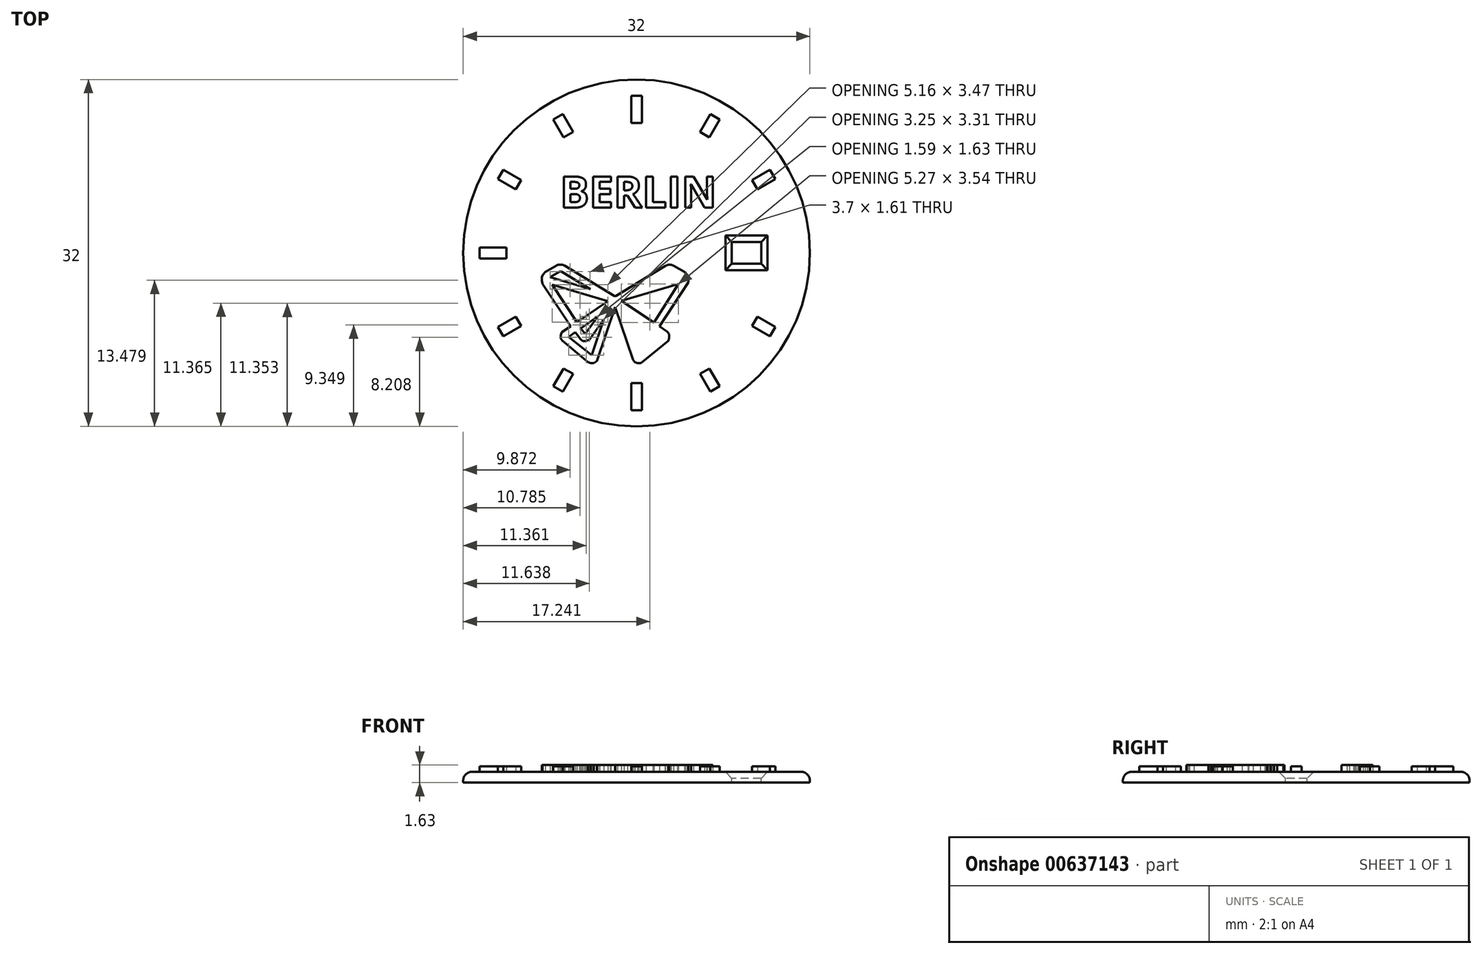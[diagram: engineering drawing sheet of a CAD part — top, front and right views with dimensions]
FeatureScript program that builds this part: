
annotation { "Feature Type Name" : "Feature", "Feature Type Description" : "" }
export const myFeature = defineFeature(function(context is Context, id is Id, definition is map)
    precondition{}
    {
        {
            var Q0;
            Q0=qCreatedBy(makeId("Top.planeOp"),FACE);
            var sketch = newSketch(context, id + "F0", { "sketchPlane" : qUnion([Q0])});
            skCircle(sketch, "E0", {"center": v(0, 0) * mm, "radius": 16 * mm});
            skLineSegment(sketch, "E1.bottom", {"start": v(8.8, 1) * mm, "end": v(11.5, 1) * mm});
            skLineSegment(sketch, "E1.top", {"start": v(8.8, -1) * mm, "end": v(11.5, -1) * mm});
            skLineSegment(sketch, "E1.left", {"start": v(8.8, 1) * mm, "end": v(8.8, -1) * mm});
            skLineSegment(sketch, "E1.right", {"start": v(11.5, 1) * mm, "end": v(11.5, -1) * mm});
            skLineSegment(sketch, "E2", {"start": v(-4.51, -9.01) * mm, "end": v(-7.42, -4.68) * mm});
            skLineSegment(sketch, "E3", {"start": v(-3.9, -8.61) * mm, "end": v(-0.72, -6.47) * mm});
            skLineSegment(sketch, "E4", {"start": v(-0.72, -6.47) * mm, "end": v(-6.45, -4.76) * mm});
            skLineSegment(sketch, "E5", {"start": v(-6.45, -4.76) * mm, "end": v(-3.9, -8.61) * mm});
            skLineSegment(sketch, "E6", {"start": v(-4.51, -9.01) * mm, "end": v(-5.44, -9.64) * mm});
            skLineSegment(sketch, "E7", {"start": v(-5.44, -9.64) * mm, "end": v(-5.54, -9.96) * mm});
            skLineSegment(sketch, "E8", {"start": v(-5.54, -9.96) * mm, "end": v(-5.54, -10.28) * mm});
            skLineSegment(sketch, "E9", {"start": v(-5.54, -10.28) * mm, "end": v(-5.38, -10.52) * mm});
            skLineSegment(sketch, "E10", {"start": v(-5.38, -10.52) * mm, "end": v(-2.76, -12.7) * mm});
            skLineSegment(sketch, "E11", {"start": v(-2.76, -12.7) * mm, "end": v(-2.48, -12.79) * mm});
            skLineSegment(sketch, "E12", {"start": v(-2.48, -12.79) * mm, "end": v(-2.15, -12.79) * mm});
            skLineSegment(sketch, "E13", {"start": v(-2.15, -12.79) * mm, "end": v(-1.84, -12.58) * mm});
            skLineSegment(sketch, "E14", {"start": v(-1.84, -12.58) * mm, "end": v(0.02, -7.06) * mm});
            skLineSegment(sketch, "E15", {"start": v(0.02, -7.06) * mm, "end": v(1.87, -12.45) * mm});
            skLineSegment(sketch, "E16", {"start": v(2.04, -12.7) * mm, "end": v(2.32, -12.79) * mm});
            skLineSegment(sketch, "E17", {"start": v(2.32, -12.79) * mm, "end": v(2.68, -12.79) * mm});
            skLineSegment(sketch, "E18", {"start": v(2.68, -12.79) * mm, "end": v(5.48, -10.52) * mm});
            skLineSegment(sketch, "E19", {"start": v(5.48, -10.52) * mm, "end": v(5.57, -10.22) * mm});
            skLineSegment(sketch, "E20", {"start": v(5.57, -10.22) * mm, "end": v(5.57, -9.85) * mm});
            skLineSegment(sketch, "E21", {"start": v(5.57, -9.85) * mm, "end": v(5.4, -9.58) * mm});
            skLineSegment(sketch, "E22", {"start": v(5.4, -9.58) * mm, "end": v(4.59, -9.01) * mm});
            skLineSegment(sketch, "E23", {"start": v(4.59, -9.01) * mm, "end": v(7.53, -4.5) * mm});
            skLineSegment(sketch, "E24", {"start": v(7.53, -4.5) * mm, "end": v(7.53, -4.14) * mm});
            skLineSegment(sketch, "E25", {"start": v(7.53, -4.14) * mm, "end": v(7.4, -3.8) * mm});
            skLineSegment(sketch, "E26", {"start": v(7.4, -3.8) * mm, "end": v(7.17, -3.47) * mm});
            skLineSegment(sketch, "E27", {"start": v(7.17, -3.47) * mm, "end": v(6.04, -2.83) * mm});
            skLineSegment(sketch, "E28", {"start": v(6.04, -2.83) * mm, "end": v(5.8, -2.7) * mm});
            skLineSegment(sketch, "E29", {"start": v(5.8, -2.7) * mm, "end": v(5.47, -2.7) * mm});
            skLineSegment(sketch, "E30", {"start": v(5.47, -2.7) * mm, "end": v(5.14, -2.84) * mm});
            skLineSegment(sketch, "E31", {"start": v(5.14, -2.84) * mm, "end": v(0.1, -5.92) * mm});
            skLineSegment(sketch, "E32", {"start": v(0.1, -5.92) * mm, "end": v(-0.04, -5.92) * mm});
            skLineSegment(sketch, "E33", {"start": v(-0.04, -5.92) * mm, "end": v(-5.14, -2.83) * mm});
            skLineSegment(sketch, "E34", {"start": v(-5.14, -2.83) * mm, "end": v(-5.37, -2.73) * mm});
            skLineSegment(sketch, "E35", {"start": v(-5.82, -2.73) * mm, "end": v(-7.14, -3.45) * mm});
            skLineSegment(sketch, "E36", {"start": v(-7.14, -3.45) * mm, "end": v(-7.4, -3.73) * mm});
            skLineSegment(sketch, "E37", {"start": v(-7.4, -3.73) * mm, "end": v(-7.5, -4) * mm});
            skLineSegment(sketch, "E38", {"start": v(-7.5, -4) * mm, "end": v(-7.5, -4.33) * mm});
            skLineSegment(sketch, "E39", {"start": v(-7.5, -4.33) * mm, "end": v(-7.42, -4.68) * mm});
            skLineSegment(sketch, "E40", {"start": v(-2.53, -5.2) * mm, "end": v(-6.64, -4) * mm});
            skLineSegment(sketch, "E41", {"start": v(-6.64, -4) * mm, "end": v(-5.65, -3.42) * mm});
            skLineSegment(sketch, "E42", {"start": v(-5.65, -3.42) * mm, "end": v(-5.47, -3.42) * mm});
            skLineSegment(sketch, "E43", {"start": v(-5.47, -3.42) * mm, "end": v(-2.53, -5.2) * mm});
            skLineSegment(sketch, "E44", {"start": v(0.76, -6.46) * mm, "end": v(6.62, -4.75) * mm});
            skLineSegment(sketch, "E45", {"start": v(6.62, -4.75) * mm, "end": v(4.1, -8.68) * mm});
            skLineSegment(sketch, "E46", {"start": v(4.1, -8.68) * mm, "end": v(0.76, -6.46) * mm});
            skLineSegment(sketch, "E47", {"start": v(-1.74, -7.99) * mm, "end": v(-3.04, -9.8) * mm});
            skLineSegment(sketch, "E48", {"start": v(-3.04, -9.8) * mm, "end": v(-3.52, -9.22) * mm});
            skLineSegment(sketch, "E49", {"start": v(-3.52, -9.22) * mm, "end": v(-1.74, -7.99) * mm});
            skLineSegment(sketch, "E50", {"start": v(-1.12, -8.33) * mm, "end": v(-2.36, -12) * mm});
            skLineSegment(sketch, "E51", {"start": v(-2.36, -12) * mm, "end": v(-4.74, -10.12) * mm});
            skLineSegment(sketch, "E52", {"start": v(-4.74, -10.12) * mm, "end": v(-4.07, -9.61) * mm});
            skLineSegment(sketch, "E53", {"start": v(-4.07, -9.61) * mm, "end": v(-3.5, -10.36) * mm});
            skLineSegment(sketch, "E54", {"start": v(-3.5, -10.36) * mm, "end": v(-3.27, -10.54) * mm});
            skLineSegment(sketch, "E55", {"start": v(-3.27, -10.54) * mm, "end": v(-2.97, -10.54) * mm});
            skLineSegment(sketch, "E56", {"start": v(-2.97, -10.54) * mm, "end": v(-2.59, -10.36) * mm});
            skLineSegment(sketch, "E57", {"start": v(-2.59, -10.36) * mm, "end": v(-1.12, -8.33) * mm});
            skLineSegment(sketch, "E58", {"start": v(-5.82, -2.73) * mm, "end": v(-5.37, -2.73) * mm});
            skLineSegment(sketch, "E59", {"start": v(0, 0) * mm, "end": v(0, 16) * mm});
            skText(sketch, "E60", { "text": "BERLIN", "fontName": "OpenSans-Bold.ttf"});
            const initialGuessF0  = {"E60": [-0.01023, 0.00388, 1, 0, 0.00412]};
            skSetInitialGuess(sketch, initialGuessF0);
            skSolve(sketch);
        }
        {
            var Q0;
            Q0=makeQuery(id+"F0.imprint","IMPRINT",FACE,{"disambiguationData":[TD([[makeQuery(id+"F0.imprint","IMPRINT",EDGE,{"derivedFrom":sQuery(id+"F0.wireOp",EDGE,"E0")}),1.0]])]});
            var Q1;
            Q1=makeQuery(id+"F0.imprint","IMPRINT",FACE,{"disambiguationData":[TD([[makeQuery(id+"F0.imprint","IMPRINT",EDGE,{"derivedFrom":sQuery(id+"F0.wireOp",EDGE,"E60.sketch_text.stroke-66")}),-1.0]])]});
            var Q2;
            Q2=makeQuery(id+"F0.imprint","IMPRINT",FACE,{"disambiguationData":[TD([[makeQuery(id+"F0.imprint","IMPRINT",EDGE,{"derivedFrom":sQuery(id+"F0.wireOp",EDGE,"E50")}),-1.0]])]});
            var Q3;
            Q3=makeQuery(id+"F0.imprint","IMPRINT",FACE,{"disambiguationData":[TD([[makeQuery(id+"F0.imprint","IMPRINT",EDGE,{"derivedFrom":sQuery(id+"F0.wireOp",EDGE,"E60.sketch_text.stroke-0")}),-1.0]])]});
            var Q4;
            Q4=makeQuery(id+"F0.imprint","IMPRINT",FACE,{"disambiguationData":[TD([[makeQuery(id+"F0.imprint","IMPRINT",EDGE,{"derivedFrom":sQuery(id+"F0.wireOp",EDGE,"E3")}),1.0]])]});
            var Q5;
            Q5=makeQuery(id+"F0.imprint","IMPRINT",FACE,{"disambiguationData":[TD([[makeQuery(id+"F0.imprint","IMPRINT",EDGE,{"derivedFrom":sQuery(id+"F0.wireOp",EDGE,"E40")}),-1.0]])]});
            var Q6;
            Q6=makeQuery(id+"F0.imprint","IMPRINT",FACE,{"disambiguationData":[TD([[makeQuery(id+"F0.imprint","IMPRINT",EDGE,{"derivedFrom":sQuery(id+"F0.wireOp",EDGE,"E60.sketch_text.stroke-12")}),1.0]])]});
            var Q7;
            {var subQ5=sQuery(id+"F0.wireOp",EDGE,"E60.sketch_text.stroke-51");Q7=makeQuery(id+"F0.imprint","IMPRINT",FACE,{"disambiguationData":[TD([[makeQuery(id+"F0.imprint","IMPRINT",EDGE,{"derivedFrom":subQ5}),1.0]])]});}
            var Q8;
            Q8=makeQuery(id+"F0.imprint","IMPRINT",FACE,{"disambiguationData":[TD([[makeQuery(id+"F0.imprint","IMPRINT",EDGE,{"derivedFrom":sQuery(id+"F0.wireOp",EDGE,"E60.sketch_text.stroke-56")}),-1.0]])]});
            var Q9;
            Q9=makeQuery(id+"F0.imprint","IMPRINT",FACE,{"disambiguationData":[TD([[makeQuery(id+"F0.imprint","IMPRINT",EDGE,{"derivedFrom":sQuery(id+"F0.wireOp",EDGE,"E60.sketch_text.stroke-62")}),-1.0]])]});
            var Q10;
            Q10=makeQuery(id+"F0.imprint","IMPRINT",FACE,{"disambiguationData":[TD([[makeQuery(id+"F0.imprint","IMPRINT",EDGE,{"derivedFrom":sQuery(id+"F0.wireOp",EDGE,"E60.sketch_text.stroke-25")}),-1.0]])]});
            var Q11;
            Q11=makeQuery(id+"F0.imprint","IMPRINT",FACE,{"disambiguationData":[TD([[makeQuery(id+"F0.imprint","IMPRINT",EDGE,{"derivedFrom":sQuery(id+"F0.wireOp",EDGE,"E60.sketch_text.stroke-37")}),-1.0]])]});
            var Q12;
            Q12=makeQuery(id+"F0.imprint","IMPRINT",FACE,{"disambiguationData":[TD([[makeQuery(id+"F0.imprint","IMPRINT",EDGE,{"derivedFrom":sQuery(id+"F0.wireOp",EDGE,"E60.sketch_text.stroke-19")}),1.0]])]});
            var Q13;
            Q13=makeQuery(id+"F0.imprint","IMPRINT",FACE,{"disambiguationData":[TD([[makeQuery(id+"F0.imprint","IMPRINT",EDGE,{"derivedFrom":sQuery(id+"F0.wireOp",EDGE,"E60.sketch_text.stroke-37")}),1.0]])]});
            var Q14;
            Q14=makeQuery(id+"F0.imprint","IMPRINT",FACE,{"disambiguationData":[TD([[makeQuery(id+"F0.imprint","IMPRINT",EDGE,{"derivedFrom":sQuery(id+"F0.wireOp",EDGE,"E44")}),-1.0]])]});
            var Q15;
            Q15=makeQuery(id+"F0.imprint","IMPRINT",FACE,{"disambiguationData":[TD([[makeQuery(id+"F0.imprint","IMPRINT",EDGE,{"derivedFrom":sQuery(id+"F0.wireOp",EDGE,"E47")}),-1.0]])]});
            var Q16;
            {var subQ0=sQuery(id+"F0.wireOp",EDGE,"E60.sketch_text.stroke-49");var subQ1=sQuery(id+"F0.wireOp",EDGE,"E59");var subQ2=makeQuery(id+"F0.imprint","INTERSECT",VERTEX,{"derivedFrom":[subQ1,subQ0]});Q16=makeQuery(id+"F0.imprint","IMPRINT",FACE,{"disambiguationData":[TD([[makeQuery(id+"F0.imprint","IMPRINT",EDGE,{"disambiguationData":[TD([[subQ2,1.0]])],"derivedFrom":subQ1}),-1.0]])]});}
            var Q17;
            {var subQ0=sQuery(id+"F0.wireOp",EDGE,"E60.sketch_text.stroke-53");var subQ1=sQuery(id+"F0.wireOp",EDGE,"E59");var subQ2=makeQuery(id+"F0.imprint","INTERSECT",VERTEX,{"derivedFrom":[subQ1,subQ0]});Q17=makeQuery(id+"F0.imprint","IMPRINT",FACE,{"disambiguationData":[TD([[makeQuery(id+"F0.imprint","IMPRINT",EDGE,{"disambiguationData":[TD([[subQ2,-1.0]])],"derivedFrom":subQ1}),-1.0]])]});}
            extrude(context, id + "F1", {"entities" : qUnion([Q0, Q1, Q2, Q3, Q4, Q5, Q6, Q7, Q8, Q9, Q10, Q11, Q12, Q13, Q14, Q15, Q16, Q17]), "oppositeDirection" : true, "depth" : 1 * mm, "offsetDistance" : 25 * mm});
        }
        {
            var Q0;
            Q0=qCreatedBy(makeId("Top.planeOp"),FACE);
            var sketch = newSketch(context, id + "F2", { "sketchPlane" : qUnion([Q0])});
            skLineSegment(sketch, "E61", {"start": v(-6.74, -7.5) * mm, "end": v(-9.65, -3.17) * mm});
            skLineSegment(sketch, "E62", {"start": v(-6.1, -7.1) * mm, "end": v(-2.93, -4.95) * mm});
            skLineSegment(sketch, "E63", {"start": v(-2.93, -4.95) * mm, "end": v(-8.66, -3.24) * mm});
            skLineSegment(sketch, "E64", {"start": v(-8.66, -3.24) * mm, "end": v(-6.1, -7.1) * mm});
            skLineSegment(sketch, "E65", {"start": v(-6.74, -7.5) * mm, "end": v(-7.67, -8.13) * mm});
            skLineSegment(sketch, "E66", {"start": v(-7.67, -8.13) * mm, "end": v(-7.76, -8.45) * mm});
            skLineSegment(sketch, "E67", {"start": v(-7.76, -8.45) * mm, "end": v(-7.76, -8.78) * mm});
            skLineSegment(sketch, "E68", {"start": v(-7.76, -8.78) * mm, "end": v(-7.6, -9) * mm});
            skLineSegment(sketch, "E69", {"start": v(-7.6, -9) * mm, "end": v(-4.99, -11.2) * mm});
            skLineSegment(sketch, "E70", {"start": v(-4.99, -11.2) * mm, "end": v(-4.7, -11.28) * mm});
            skLineSegment(sketch, "E71", {"start": v(-4.7, -11.28) * mm, "end": v(-4.37, -11.28) * mm});
            skLineSegment(sketch, "E72", {"start": v(-4.37, -11.28) * mm, "end": v(-4.06, -11.07) * mm});
            skLineSegment(sketch, "E73", {"start": v(-4.06, -11.07) * mm, "end": v(-2.2, -5.55) * mm});
            skLineSegment(sketch, "E74", {"start": v(-2.2, -5.55) * mm, "end": v(-0.36, -10.94) * mm});
            skLineSegment(sketch, "E75", {"start": v(-0.19, -11.2) * mm, "end": v(0.1, -11.28) * mm});
            skLineSegment(sketch, "E76", {"start": v(0.1, -11.28) * mm, "end": v(0.45, -11.28) * mm});
            skLineSegment(sketch, "E77", {"start": v(0.45, -11.28) * mm, "end": v(3.26, -9) * mm});
            skLineSegment(sketch, "E78", {"start": v(3.26, -9) * mm, "end": v(3.35, -8.71) * mm});
            skLineSegment(sketch, "E79", {"start": v(3.35, -8.71) * mm, "end": v(3.35, -8.34) * mm});
            skLineSegment(sketch, "E80", {"start": v(3.35, -8.34) * mm, "end": v(3.17, -8.07) * mm});
            skLineSegment(sketch, "E81", {"start": v(3.17, -8.07) * mm, "end": v(2.36, -7.5) * mm});
            skLineSegment(sketch, "E82", {"start": v(2.36, -7.5) * mm, "end": v(5.3, -3) * mm});
            skLineSegment(sketch, "E83", {"start": v(5.3, -3) * mm, "end": v(5.3, -2.63) * mm});
            skLineSegment(sketch, "E84", {"start": v(5.3, -2.63) * mm, "end": v(5.17, -2.29) * mm});
            skLineSegment(sketch, "E85", {"start": v(5.17, -2.29) * mm, "end": v(4.94, -1.96) * mm});
            skLineSegment(sketch, "E86", {"start": v(4.94, -1.96) * mm, "end": v(3.8, -1.32) * mm});
            skLineSegment(sketch, "E87", {"start": v(3.8, -1.32) * mm, "end": v(3.57, -1.2) * mm});
            skLineSegment(sketch, "E88", {"start": v(3.57, -1.2) * mm, "end": v(3.24, -1.2) * mm});
            skLineSegment(sketch, "E89", {"start": v(3.24, -1.2) * mm, "end": v(2.91, -1.33) * mm});
            skLineSegment(sketch, "E90", {"start": v(2.91, -1.33) * mm, "end": v(-2.12, -4.41) * mm});
            skLineSegment(sketch, "E91", {"start": v(-2.12, -4.41) * mm, "end": v(-2.27, -4.41) * mm});
            skLineSegment(sketch, "E92", {"start": v(-2.27, -4.41) * mm, "end": v(-7.37, -1.32) * mm});
            skLineSegment(sketch, "E93", {"start": v(-7.37, -1.32) * mm, "end": v(-7.6, -1.21) * mm});
            skLineSegment(sketch, "E94", {"start": v(-8.05, -1.21) * mm, "end": v(-9.37, -1.94) * mm});
            skLineSegment(sketch, "E95", {"start": v(-9.37, -1.94) * mm, "end": v(-9.62, -2.22) * mm});
            skLineSegment(sketch, "E96", {"start": v(-9.62, -2.22) * mm, "end": v(-9.73, -2.49) * mm});
            skLineSegment(sketch, "E97", {"start": v(-9.73, -2.49) * mm, "end": v(-9.73, -2.83) * mm});
            skLineSegment(sketch, "E98", {"start": v(-9.73, -2.83) * mm, "end": v(-9.65, -3.17) * mm});
            skLineSegment(sketch, "E99", {"start": v(-4.76, -3.7) * mm, "end": v(-8.86, -2.49) * mm});
            skLineSegment(sketch, "E100", {"start": v(-8.86, -2.49) * mm, "end": v(-7.87, -1.9) * mm});
            skLineSegment(sketch, "E101", {"start": v(-7.87, -1.9) * mm, "end": v(-7.7, -1.9) * mm});
            skLineSegment(sketch, "E102", {"start": v(-7.7, -1.9) * mm, "end": v(-4.76, -3.7) * mm});
            skLineSegment(sketch, "E103", {"start": v(-1.55, -4.9) * mm, "end": v(4.3, -3.18) * mm});
            skLineSegment(sketch, "E104", {"start": v(4.3, -3.18) * mm, "end": v(1.78, -7.12) * mm});
            skLineSegment(sketch, "E105", {"start": v(1.78, -7.12) * mm, "end": v(-1.55, -4.9) * mm});
            skLineSegment(sketch, "E106", {"start": v(-3.96, -6.49) * mm, "end": v(-5.26, -8.3) * mm});
            skLineSegment(sketch, "E107", {"start": v(-5.26, -8.3) * mm, "end": v(-5.73, -7.72) * mm});
            skLineSegment(sketch, "E108", {"start": v(-5.73, -7.72) * mm, "end": v(-3.96, -6.49) * mm});
            skLineSegment(sketch, "E109", {"start": v(-3.35, -6.82) * mm, "end": v(-4.58, -10.5) * mm});
            skLineSegment(sketch, "E110", {"start": v(-4.58, -10.5) * mm, "end": v(-6.96, -8.61) * mm});
            skLineSegment(sketch, "E111", {"start": v(-6.96, -8.61) * mm, "end": v(-6.3, -8.1) * mm});
            skLineSegment(sketch, "E112", {"start": v(-6.3, -8.1) * mm, "end": v(-5.73, -8.85) * mm});
            skLineSegment(sketch, "E113", {"start": v(-5.73, -8.85) * mm, "end": v(-5.5, -9.03) * mm});
            skLineSegment(sketch, "E114", {"start": v(-5.5, -9.03) * mm, "end": v(-5.2, -9.03) * mm});
            skLineSegment(sketch, "E115", {"start": v(-5.2, -9.03) * mm, "end": v(-4.81, -8.85) * mm});
            skLineSegment(sketch, "E116", {"start": v(-4.81, -8.85) * mm, "end": v(-3.35, -6.82) * mm});
            skLineSegment(sketch, "E117", {"start": v(-8.05, -1.21) * mm, "end": v(-7.6, -1.21) * mm});
            skText(sketch, "E118", { "text": "BERLIN", "fontName": "OpenSans-Bold.ttf"});
            skLineSegment(sketch, "E119", {"start": v(-0.19, -11.2) * mm, "end": v(-0.36, -10.94) * mm});
            const initialGuessF2  = {"E118": [-0.00787, 0.00465, 1, 0, 0.00322]};
            skSetInitialGuess(sketch, initialGuessF2);
            skSolve(sketch);
        }
        {
            var Q0;
            Q0 = qSketchRegion(id + "F2", true);
            extrude(context, id + "F3", {"entities" : qUnion([Q0]), "depth" : 0.7 * mm, "offsetDistance" : 25 * mm});
        }
        {
            var Q0;
            Q0=makeQuery(id+"F1.opExtrude","CAP_EDGE",EDGE,{"disambiguationData":[OSD([sQuery(id+"F0.wireOp",EDGE,"E1.bottom")])],"isStart":true});
            var Q1;
            Q1=makeQuery(id+"F1.opExtrude","CAP_EDGE",EDGE,{"disambiguationData":[OSD([sQuery(id+"F0.wireOp",EDGE,"E1.left")])],"isStart":true});
            var Q2;
            Q2=makeQuery(id+"F1.opExtrude","CAP_EDGE",EDGE,{"disambiguationData":[OSD([sQuery(id+"F0.wireOp",EDGE,"E1.right")])],"isStart":true});
            var Q3;
            Q3=makeQuery(id+"F1.opExtrude","CAP_EDGE",EDGE,{"disambiguationData":[OSD([sQuery(id+"F0.wireOp",EDGE,"E1.top")])],"isStart":true});
            chamfer(context, id + "F4", {"entities" : qUnion([Q0, Q1, Q2, Q3]), "width" : 0.6 * mm, "tangentPropagation" : true});
        }
        {
            var Q0;
            Q0=makeQuery(id+"F1.opExtrude","CAP_EDGE",EDGE,{"disambiguationData":[OSD([sQuery(id+"F0.wireOp",EDGE,"E0")])],"isStart":true});
            fillet(context, id + "F5", {"entities" : qUnion([Q0]), "radius" : 0.8 * mm, "tangentPropagation" : true, "allowEdgeOverflow" : false});
        }
        {
            var Q0;
            Q0=qCreatedBy(makeId("Top.planeOp"),FACE);
            var sketch = newSketch(context, id + "F6", { "sketchPlane" : qUnion([Q0])});
            skCircle(sketch, "E120.0", {"center": v(0, 0) * mm, "radius": 12 * mm});
            skCircle(sketch, "E121.0", {"center": v(0, 0) * mm, "radius": 14.5 * mm});
            skLineSegment(sketch, "E122.0", {"start": v(-12, 0.5) * mm, "end": v(-14.5, 0.5) * mm});
            skLineSegment(sketch, "E123.0", {"start": v(-12, -0.5) * mm, "end": v(-14.5, -0.5) * mm});
            skLineSegment(sketch, "E124", {"start": v(-12, 0.5) * mm, "end": v(-12, -0.5) * mm});
            skLineSegment(sketch, "E125", {"start": v(-14.5, 0.5) * mm, "end": v(-14.5, -0.5) * mm});
            skLineSegment(sketch, "E126.0", {"start": v(0.5, 12) * mm, "end": v(0.5, 14.5) * mm});
            skLineSegment(sketch, "E127.0", {"start": v(-0.5, 12) * mm, "end": v(-0.5, 14.5) * mm});
            skLineSegment(sketch, "E128", {"start": v(-0.5, 14.5) * mm, "end": v(0.5, 14.5) * mm});
            skLineSegment(sketch, "E129", {"start": v(-0.5, 12) * mm, "end": v(0.5, 12) * mm});
            skLineSegment(sketch, "E130.0", {"start": v(0.5, -14.5) * mm, "end": v(0.5, -12) * mm});
            skLineSegment(sketch, "E131.0", {"start": v(-0.5, -14.5) * mm, "end": v(-0.5, -12) * mm});
            skLineSegment(sketch, "E132", {"start": v(-0.5, -12) * mm, "end": v(0.5, -12) * mm});
            skLineSegment(sketch, "E133", {"start": v(-0.5, -14.5) * mm, "end": v(0.5, -14.5) * mm});
            skCircle(sketch, "E134.0", {"center": v(0, 0) * mm, "radius": 12.6 * mm});
            skLineSegment(sketch, "E135.0", {"start": v(-5.87, -11.16) * mm, "end": v(-6.82, -12.8) * mm});
            skLineSegment(sketch, "E136.0", {"start": v(-6.73, -10.66) * mm, "end": v(-7.68, -12.3) * mm});
            skLineSegment(sketch, "E137.0", {"start": v(-11.16, -5.87) * mm, "end": v(-12.8, -6.82) * mm});
            skLineSegment(sketch, "E138.0", {"start": v(-10.66, -6.73) * mm, "end": v(-12.3, -7.68) * mm});
            skLineSegment(sketch, "E139", {"start": v(-12.3, -7.68) * mm, "end": v(-12.8, -6.82) * mm});
            skLineSegment(sketch, "E140", {"start": v(-11.16, -5.87) * mm, "end": v(-10.66, -6.73) * mm});
            skLineSegment(sketch, "E141", {"start": v(-7.68, -12.3) * mm, "end": v(-6.82, -12.8) * mm});
            skLineSegment(sketch, "E142", {"start": v(-6.73, -10.66) * mm, "end": v(-5.87, -11.16) * mm});
            skLineSegment(sketch, "E143", {"start": v(-6.82, -12.8) * mm, "end": v(-7.68, -12.3) * mm});
            skLineSegment(sketch, "E144.0", {"start": v(5.87, -11.16) * mm, "end": v(6.82, -12.8) * mm});
            skLineSegment(sketch, "E145.0", {"start": v(6.73, -10.66) * mm, "end": v(7.68, -12.3) * mm});
            skLineSegment(sketch, "E146.0", {"start": v(10.66, -6.73) * mm, "end": v(12.3, -7.68) * mm});
            skLineSegment(sketch, "E147.0", {"start": v(11.16, -5.87) * mm, "end": v(12.8, -6.82) * mm});
            skLineSegment(sketch, "E148.0", {"start": v(6.73, 10.66) * mm, "end": v(7.68, 12.3) * mm});
            skLineSegment(sketch, "E149.0", {"start": v(5.87, 11.16) * mm, "end": v(6.82, 12.8) * mm});
            skLineSegment(sketch, "E150.0", {"start": v(11.16, 5.87) * mm, "end": v(12.8, 6.82) * mm});
            skLineSegment(sketch, "E151.0", {"start": v(10.66, 6.73) * mm, "end": v(12.3, 7.68) * mm});
            skLineSegment(sketch, "E152.0", {"start": v(-5.87, 11.16) * mm, "end": v(-6.82, 12.8) * mm});
            skLineSegment(sketch, "E153.0", {"start": v(-6.73, 10.66) * mm, "end": v(-7.68, 12.3) * mm});
            skLineSegment(sketch, "E154.0", {"start": v(-10.66, 6.73) * mm, "end": v(-12.3, 7.68) * mm});
            skLineSegment(sketch, "E155.0", {"start": v(-11.16, 5.87) * mm, "end": v(-12.8, 6.82) * mm});
            skLineSegment(sketch, "E156", {"start": v(-12.8, 6.82) * mm, "end": v(-12.3, 7.68) * mm});
            skLineSegment(sketch, "E157", {"start": v(-11.16, 5.87) * mm, "end": v(-10.66, 6.73) * mm});
            skLineSegment(sketch, "E158", {"start": v(-7.68, 12.3) * mm, "end": v(-6.82, 12.8) * mm});
            skLineSegment(sketch, "E159", {"start": v(-6.73, 10.66) * mm, "end": v(-5.87, 11.16) * mm});
            skLineSegment(sketch, "E160", {"start": v(5.87, 11.16) * mm, "end": v(6.73, 10.66) * mm});
            skLineSegment(sketch, "E161", {"start": v(6.82, 12.8) * mm, "end": v(7.68, 12.3) * mm});
            skLineSegment(sketch, "E162", {"start": v(10.66, 6.73) * mm, "end": v(11.16, 5.87) * mm});
            skLineSegment(sketch, "E163", {"start": v(12.3, 7.68) * mm, "end": v(12.8, 6.82) * mm});
            skLineSegment(sketch, "E164", {"start": v(11.16, -5.87) * mm, "end": v(10.66, -6.73) * mm});
            skLineSegment(sketch, "E165", {"start": v(12.3, -7.68) * mm, "end": v(12.8, -6.82) * mm});
            skLineSegment(sketch, "E166", {"start": v(5.87, -11.16) * mm, "end": v(6.73, -10.66) * mm});
            skLineSegment(sketch, "E167", {"start": v(6.82, -12.8) * mm, "end": v(7.68, -12.3) * mm});
            skSolve(sketch);
        }
        {
            var Q0;
            Q0=makeQuery(id+"F3.opExtrude","SWEPT_BODY",BODY,{"disambiguationData":[OSD([sQuery(id+"F2.wireOp",EDGE,"E61"),sQuery(id+"F2.wireOp",EDGE,"E62"),sQuery(id+"F2.wireOp",EDGE,"E63"),sQuery(id+"F2.wireOp",EDGE,"E64"),sQuery(id+"F2.wireOp",EDGE,"E65"),sQuery(id+"F2.wireOp",EDGE,"E66"),sQuery(id+"F2.wireOp",EDGE,"E67"),sQuery(id+"F2.wireOp",EDGE,"E68"),sQuery(id+"F2.wireOp",EDGE,"E69"),sQuery(id+"F2.wireOp",EDGE,"E70"),sQuery(id+"F2.wireOp",EDGE,"E71"),sQuery(id+"F2.wireOp",EDGE,"E72"),sQuery(id+"F2.wireOp",EDGE,"E73"),sQuery(id+"F2.wireOp",EDGE,"E74"),sQuery(id+"F2.wireOp",EDGE,"E75"),sQuery(id+"F2.wireOp",EDGE,"E76"),sQuery(id+"F2.wireOp",EDGE,"E77"),sQuery(id+"F2.wireOp",EDGE,"E78"),sQuery(id+"F2.wireOp",EDGE,"E79"),sQuery(id+"F2.wireOp",EDGE,"E80"),sQuery(id+"F2.wireOp",EDGE,"E81"),sQuery(id+"F2.wireOp",EDGE,"E82"),sQuery(id+"F2.wireOp",EDGE,"E83"),sQuery(id+"F2.wireOp",EDGE,"E84"),sQuery(id+"F2.wireOp",EDGE,"E85"),sQuery(id+"F2.wireOp",EDGE,"E86"),sQuery(id+"F2.wireOp",EDGE,"E87"),sQuery(id+"F2.wireOp",EDGE,"E88"),sQuery(id+"F2.wireOp",EDGE,"E89"),sQuery(id+"F2.wireOp",EDGE,"E90"),sQuery(id+"F2.wireOp",EDGE,"E91"),sQuery(id+"F2.wireOp",EDGE,"E92"),sQuery(id+"F2.wireOp",EDGE,"E93"),sQuery(id+"F2.wireOp",EDGE,"E94"),sQuery(id+"F2.wireOp",EDGE,"E95"),sQuery(id+"F2.wireOp",EDGE,"E96"),sQuery(id+"F2.wireOp",EDGE,"E97"),sQuery(id+"F2.wireOp",EDGE,"E98"),sQuery(id+"F2.wireOp",EDGE,"E99"),sQuery(id+"F2.wireOp",EDGE,"E100"),sQuery(id+"F2.wireOp",EDGE,"E101"),sQuery(id+"F2.wireOp",EDGE,"E102"),sQuery(id+"F2.wireOp",EDGE,"E103"),sQuery(id+"F2.wireOp",EDGE,"E104"),sQuery(id+"F2.wireOp",EDGE,"E105"),sQuery(id+"F2.wireOp",EDGE,"E106"),sQuery(id+"F2.wireOp",EDGE,"E107"),sQuery(id+"F2.wireOp",EDGE,"E108"),sQuery(id+"F2.wireOp",EDGE,"E109"),sQuery(id+"F2.wireOp",EDGE,"E110"),sQuery(id+"F2.wireOp",EDGE,"E111"),sQuery(id+"F2.wireOp",EDGE,"E112"),sQuery(id+"F2.wireOp",EDGE,"E113"),sQuery(id+"F2.wireOp",EDGE,"E114"),sQuery(id+"F2.wireOp",EDGE,"E115"),sQuery(id+"F2.wireOp",EDGE,"E116"),sQuery(id+"F2.wireOp",EDGE,"E117"),sQuery(id+"F2.wireOp",EDGE,"E119")])]});
            var Q1;
            Q1=qCreatedBy(makeId("Origin.pointOp"),VERTEX);
            transform(context, id + "F7", {"entities" : qUnion([Q0]), "transformType" : TransformType.SCALE_UNIFORMLY, "scale" : 0.9, "scalePoint" : qUnion([Q1]), "makeCopy" : false});
        }
        {
            var Q0;
            Q0=makeQuery(id+"F3.opExtrude","SWEPT_BODY",BODY,{"disambiguationData":[OSD([sQuery(id+"F2.wireOp",EDGE,"E118.sketch_text.stroke-0"),sQuery(id+"F2.wireOp",EDGE,"E118.sketch_text.stroke-1"),sQuery(id+"F2.wireOp",EDGE,"E118.sketch_text.stroke-2"),sQuery(id+"F2.wireOp",EDGE,"E118.sketch_text.stroke-3"),sQuery(id+"F2.wireOp",EDGE,"E118.sketch_text.stroke-4"),sQuery(id+"F2.wireOp",EDGE,"E118.sketch_text.stroke-5"),sQuery(id+"F2.wireOp",EDGE,"E118.sketch_text.stroke-6"),sQuery(id+"F2.wireOp",EDGE,"E118.sketch_text.stroke-7"),sQuery(id+"F2.wireOp",EDGE,"E118.sketch_text.stroke-8"),sQuery(id+"F2.wireOp",EDGE,"E118.sketch_text.stroke-9"),sQuery(id+"F2.wireOp",EDGE,"E118.sketch_text.stroke-10"),sQuery(id+"F2.wireOp",EDGE,"E118.sketch_text.stroke-11"),sQuery(id+"F2.wireOp",EDGE,"E118.sketch_text.stroke-12"),sQuery(id+"F2.wireOp",EDGE,"E118.sketch_text.stroke-13"),sQuery(id+"F2.wireOp",EDGE,"E118.sketch_text.stroke-14"),sQuery(id+"F2.wireOp",EDGE,"E118.sketch_text.stroke-15"),sQuery(id+"F2.wireOp",EDGE,"E118.sketch_text.stroke-16"),sQuery(id+"F2.wireOp",EDGE,"E118.sketch_text.stroke-17"),sQuery(id+"F2.wireOp",EDGE,"E118.sketch_text.stroke-18"),sQuery(id+"F2.wireOp",EDGE,"E118.sketch_text.stroke-19"),sQuery(id+"F2.wireOp",EDGE,"E118.sketch_text.stroke-20"),sQuery(id+"F2.wireOp",EDGE,"E118.sketch_text.stroke-21"),sQuery(id+"F2.wireOp",EDGE,"E118.sketch_text.stroke-22"),sQuery(id+"F2.wireOp",EDGE,"E118.sketch_text.stroke-23"),sQuery(id+"F2.wireOp",EDGE,"E118.sketch_text.stroke-24")])]});
            var Q1;
            Q1=makeQuery(id+"F3.opExtrude","SWEPT_BODY",BODY,{"disambiguationData":[OSD([sQuery(id+"F2.wireOp",EDGE,"E118.sketch_text.stroke-25"),sQuery(id+"F2.wireOp",EDGE,"E118.sketch_text.stroke-26"),sQuery(id+"F2.wireOp",EDGE,"E118.sketch_text.stroke-27"),sQuery(id+"F2.wireOp",EDGE,"E118.sketch_text.stroke-28"),sQuery(id+"F2.wireOp",EDGE,"E118.sketch_text.stroke-29"),sQuery(id+"F2.wireOp",EDGE,"E118.sketch_text.stroke-30"),sQuery(id+"F2.wireOp",EDGE,"E118.sketch_text.stroke-31"),sQuery(id+"F2.wireOp",EDGE,"E118.sketch_text.stroke-32"),sQuery(id+"F2.wireOp",EDGE,"E118.sketch_text.stroke-33"),sQuery(id+"F2.wireOp",EDGE,"E118.sketch_text.stroke-34"),sQuery(id+"F2.wireOp",EDGE,"E118.sketch_text.stroke-35"),sQuery(id+"F2.wireOp",EDGE,"E118.sketch_text.stroke-36")])]});
            var Q2;
            Q2=makeQuery(id+"F3.opExtrude","SWEPT_BODY",BODY,{"disambiguationData":[OSD([sQuery(id+"F2.wireOp",EDGE,"E118.sketch_text.stroke-37"),sQuery(id+"F2.wireOp",EDGE,"E118.sketch_text.stroke-38"),sQuery(id+"F2.wireOp",EDGE,"E118.sketch_text.stroke-39"),sQuery(id+"F2.wireOp",EDGE,"E118.sketch_text.stroke-40"),sQuery(id+"F2.wireOp",EDGE,"E118.sketch_text.stroke-41"),sQuery(id+"F2.wireOp",EDGE,"E118.sketch_text.stroke-42"),sQuery(id+"F2.wireOp",EDGE,"E118.sketch_text.stroke-43"),sQuery(id+"F2.wireOp",EDGE,"E118.sketch_text.stroke-44"),sQuery(id+"F2.wireOp",EDGE,"E118.sketch_text.stroke-45"),sQuery(id+"F2.wireOp",EDGE,"E118.sketch_text.stroke-46"),sQuery(id+"F2.wireOp",EDGE,"E118.sketch_text.stroke-47"),sQuery(id+"F2.wireOp",EDGE,"E118.sketch_text.stroke-48"),sQuery(id+"F2.wireOp",EDGE,"E118.sketch_text.stroke-49"),sQuery(id+"F2.wireOp",EDGE,"E118.sketch_text.stroke-50"),sQuery(id+"F2.wireOp",EDGE,"E118.sketch_text.stroke-51"),sQuery(id+"F2.wireOp",EDGE,"E118.sketch_text.stroke-52"),sQuery(id+"F2.wireOp",EDGE,"E118.sketch_text.stroke-53"),sQuery(id+"F2.wireOp",EDGE,"E118.sketch_text.stroke-54"),sQuery(id+"F2.wireOp",EDGE,"E118.sketch_text.stroke-55")])]});
            var Q3;
            Q3=makeQuery(id+"F3.opExtrude","SWEPT_BODY",BODY,{"disambiguationData":[OSD([sQuery(id+"F2.wireOp",EDGE,"E118.sketch_text.stroke-56"),sQuery(id+"F2.wireOp",EDGE,"E118.sketch_text.stroke-57"),sQuery(id+"F2.wireOp",EDGE,"E118.sketch_text.stroke-58"),sQuery(id+"F2.wireOp",EDGE,"E118.sketch_text.stroke-59"),sQuery(id+"F2.wireOp",EDGE,"E118.sketch_text.stroke-60"),sQuery(id+"F2.wireOp",EDGE,"E118.sketch_text.stroke-61")])]});
            var Q4;
            Q4=makeQuery(id+"F3.opExtrude","SWEPT_BODY",BODY,{"disambiguationData":[OSD([sQuery(id+"F2.wireOp",EDGE,"E118.sketch_text.stroke-62"),sQuery(id+"F2.wireOp",EDGE,"E118.sketch_text.stroke-63"),sQuery(id+"F2.wireOp",EDGE,"E118.sketch_text.stroke-64"),sQuery(id+"F2.wireOp",EDGE,"E118.sketch_text.stroke-65")])]});
            var Q5;
            Q5=makeQuery(id+"F3.opExtrude","SWEPT_BODY",BODY,{"disambiguationData":[OSD([sQuery(id+"F2.wireOp",EDGE,"E118.sketch_text.stroke-66"),sQuery(id+"F2.wireOp",EDGE,"E118.sketch_text.stroke-67"),sQuery(id+"F2.wireOp",EDGE,"E118.sketch_text.stroke-68"),sQuery(id+"F2.wireOp",EDGE,"E118.sketch_text.stroke-69"),sQuery(id+"F2.wireOp",EDGE,"E118.sketch_text.stroke-70"),sQuery(id+"F2.wireOp",EDGE,"E118.sketch_text.stroke-71"),sQuery(id+"F2.wireOp",EDGE,"E118.sketch_text.stroke-72"),sQuery(id+"F2.wireOp",EDGE,"E118.sketch_text.stroke-73"),sQuery(id+"F2.wireOp",EDGE,"E118.sketch_text.stroke-74"),sQuery(id+"F2.wireOp",EDGE,"E118.sketch_text.stroke-75"),sQuery(id+"F2.wireOp",EDGE,"E118.sketch_text.stroke-76"),sQuery(id+"F2.wireOp",EDGE,"E118.sketch_text.stroke-77"),sQuery(id+"F2.wireOp",EDGE,"E118.sketch_text.stroke-78"),sQuery(id+"F2.wireOp",EDGE,"E118.sketch_text.stroke-79")])]});
            var Q6;
            Q6=qCreatedBy(makeId("Origin.pointOp"),VERTEX);
            transform(context, id + "F8", {"entities" : qUnion([Q0, Q1, Q2, Q3, Q4, Q5]), "transformType" : TransformType.SCALE_UNIFORMLY, "scale" : .9, "scalePoint" : qUnion([Q6]), "makeCopy" : false});
        }
        {
            var Q0;
            {var subQ0=sQuery(id+"F6.wireOp",EDGE,"E163");var subQ1=sQuery(id+"F6.wireOp",EDGE,"E121.0");var subQ2=makeQuery(id+"F6.imprint","INTERSECT",VERTEX,{"derivedFrom":[subQ1,subQ0]});Q0=makeQuery(id+"F6.imprint","IMPRINT",FACE,{"disambiguationData":[TD([[makeQuery(id+"F6.imprint","IMPRINT",EDGE,{"disambiguationData":[TD([[subQ2,1.0]])],"derivedFrom":subQ1}),-1.0]])]});}
            var Q1;
            {var subQ0=sQuery(id+"F6.wireOp",EDGE,"E163");var subQ1=sQuery(id+"F6.wireOp",EDGE,"E121.0");var subQ2=makeQuery(id+"F6.imprint","INTERSECT",VERTEX,{"derivedFrom":[subQ1,subQ0]});Q1=makeQuery(id+"F6.imprint","IMPRINT",FACE,{"disambiguationData":[TD([[makeQuery(id+"F6.imprint","IMPRINT",EDGE,{"disambiguationData":[TD([[subQ2,-1.0]])],"derivedFrom":subQ1}),-1.0]])]});}
            var Q2;
            {var subQ0=sQuery(id+"F6.wireOp",EDGE,"E148.0");var subQ1=sQuery(id+"F6.wireOp",EDGE,"E121.0");var subQ2=makeQuery(id+"F6.imprint","INTERSECT",VERTEX,{"derivedFrom":[subQ1,subQ0]});Q2=makeQuery(id+"F6.imprint","IMPRINT",FACE,{"disambiguationData":[TD([[makeQuery(id+"F6.imprint","IMPRINT",EDGE,{"disambiguationData":[TD([[subQ2,-1.0]])],"derivedFrom":subQ1}),-1.0]])]});}
            var Q3;
            {var subQ0=sQuery(id+"F6.wireOp",EDGE,"E161");var subQ1=sQuery(id+"F6.wireOp",EDGE,"E121.0");var subQ2=makeQuery(id+"F6.imprint","INTERSECT",VERTEX,{"derivedFrom":[subQ1,subQ0]});Q3=makeQuery(id+"F6.imprint","IMPRINT",FACE,{"disambiguationData":[TD([[makeQuery(id+"F6.imprint","IMPRINT",EDGE,{"disambiguationData":[TD([[subQ2,-1.0]])],"derivedFrom":subQ1}),-1.0]])]});}
            var Q4;
            {var subQ0=sQuery(id+"F6.wireOp",EDGE,"E126.0");var subQ1=sQuery(id+"F6.wireOp",EDGE,"E121.0");var subQ2=makeQuery(id+"F6.imprint","INTERSECT",VERTEX,{"derivedFrom":[subQ1,subQ0]});Q4=makeQuery(id+"F6.imprint","IMPRINT",FACE,{"disambiguationData":[TD([[makeQuery(id+"F6.imprint","IMPRINT",EDGE,{"disambiguationData":[TD([[subQ2,-1.0]])],"derivedFrom":subQ1}),-1.0]])]});}
            var Q5;
            {var subQ0=sQuery(id+"F6.wireOp",EDGE,"E128");var subQ1=sQuery(id+"F6.wireOp",EDGE,"E121.0");var subQ2=makeQuery(id+"F6.imprint","INTERSECT",VERTEX,{"derivedFrom":[subQ1,subQ0]});Q5=makeQuery(id+"F6.imprint","IMPRINT",FACE,{"disambiguationData":[TD([[makeQuery(id+"F6.imprint","IMPRINT",EDGE,{"disambiguationData":[TD([[subQ2,-1.0]])],"derivedFrom":subQ1}),-1.0]])]});}
            var Q6;
            {var subQ0=sQuery(id+"F6.wireOp",EDGE,"E152.0");var subQ1=sQuery(id+"F6.wireOp",EDGE,"E121.0");var subQ2=makeQuery(id+"F6.imprint","INTERSECT",VERTEX,{"derivedFrom":[subQ1,subQ0]});Q6=makeQuery(id+"F6.imprint","IMPRINT",FACE,{"disambiguationData":[TD([[makeQuery(id+"F6.imprint","IMPRINT",EDGE,{"disambiguationData":[TD([[subQ2,-1.0]])],"derivedFrom":subQ1}),-1.0]])]});}
            var Q7;
            {var subQ0=sQuery(id+"F6.wireOp",EDGE,"E158");var subQ1=sQuery(id+"F6.wireOp",EDGE,"E121.0");var subQ2=makeQuery(id+"F6.imprint","INTERSECT",VERTEX,{"derivedFrom":[subQ1,subQ0]});Q7=makeQuery(id+"F6.imprint","IMPRINT",FACE,{"disambiguationData":[TD([[makeQuery(id+"F6.imprint","IMPRINT",EDGE,{"disambiguationData":[TD([[subQ2,-1.0]])],"derivedFrom":subQ1}),-1.0]])]});}
            var Q8;
            {var subQ0=sQuery(id+"F6.wireOp",EDGE,"E154.0");var subQ1=sQuery(id+"F6.wireOp",EDGE,"E121.0");var subQ2=makeQuery(id+"F6.imprint","INTERSECT",VERTEX,{"derivedFrom":[subQ1,subQ0]});Q8=makeQuery(id+"F6.imprint","IMPRINT",FACE,{"disambiguationData":[TD([[makeQuery(id+"F6.imprint","IMPRINT",EDGE,{"disambiguationData":[TD([[subQ2,-1.0]])],"derivedFrom":subQ1}),-1.0]])]});}
            var Q9;
            {var subQ0=sQuery(id+"F6.wireOp",EDGE,"E156");var subQ1=sQuery(id+"F6.wireOp",EDGE,"E121.0");var subQ2=makeQuery(id+"F6.imprint","INTERSECT",VERTEX,{"derivedFrom":[subQ1,subQ0]});Q9=makeQuery(id+"F6.imprint","IMPRINT",FACE,{"disambiguationData":[TD([[makeQuery(id+"F6.imprint","IMPRINT",EDGE,{"disambiguationData":[TD([[subQ2,-1.0]])],"derivedFrom":subQ1}),-1.0]])]});}
            var Q10;
            {var subQ0=sQuery(id+"F6.wireOp",EDGE,"E122.0");var subQ1=sQuery(id+"F6.wireOp",EDGE,"E121.0");var subQ2=makeQuery(id+"F6.imprint","INTERSECT",VERTEX,{"derivedFrom":[subQ1,subQ0]});Q10=makeQuery(id+"F6.imprint","IMPRINT",FACE,{"disambiguationData":[TD([[makeQuery(id+"F6.imprint","IMPRINT",EDGE,{"disambiguationData":[TD([[subQ2,-1.0]])],"derivedFrom":subQ1}),-1.0]])]});}
            var Q11;
            {var subQ0=sQuery(id+"F6.wireOp",EDGE,"E125");var subQ1=sQuery(id+"F6.wireOp",EDGE,"E121.0");var subQ2=makeQuery(id+"F6.imprint","INTERSECT",VERTEX,{"derivedFrom":[subQ1,subQ0]});Q11=makeQuery(id+"F6.imprint","IMPRINT",FACE,{"disambiguationData":[TD([[makeQuery(id+"F6.imprint","IMPRINT",EDGE,{"disambiguationData":[TD([[subQ2,-1.0]])],"derivedFrom":subQ1}),-1.0]])]});}
            var Q12;
            {var subQ0=sQuery(id+"F6.wireOp",EDGE,"E137.0");var subQ1=sQuery(id+"F6.wireOp",EDGE,"E121.0");var subQ2=makeQuery(id+"F6.imprint","INTERSECT",VERTEX,{"derivedFrom":[subQ1,subQ0]});Q12=makeQuery(id+"F6.imprint","IMPRINT",FACE,{"disambiguationData":[TD([[makeQuery(id+"F6.imprint","IMPRINT",EDGE,{"disambiguationData":[TD([[subQ2,-1.0]])],"derivedFrom":subQ1}),-1.0]])]});}
            var Q13;
            {var subQ0=sQuery(id+"F6.wireOp",EDGE,"E139");var subQ1=sQuery(id+"F6.wireOp",EDGE,"E121.0");var subQ2=makeQuery(id+"F6.imprint","INTERSECT",VERTEX,{"derivedFrom":[subQ1,subQ0]});Q13=makeQuery(id+"F6.imprint","IMPRINT",FACE,{"disambiguationData":[TD([[makeQuery(id+"F6.imprint","IMPRINT",EDGE,{"disambiguationData":[TD([[subQ2,-1.0]])],"derivedFrom":subQ1}),-1.0]])]});}
            var Q14;
            {var subQ0=sQuery(id+"F6.wireOp",EDGE,"E136.0");var subQ1=sQuery(id+"F6.wireOp",EDGE,"E121.0");var subQ2=makeQuery(id+"F6.imprint","INTERSECT",VERTEX,{"derivedFrom":[subQ1,subQ0]});Q14=makeQuery(id+"F6.imprint","IMPRINT",FACE,{"disambiguationData":[TD([[makeQuery(id+"F6.imprint","IMPRINT",EDGE,{"disambiguationData":[TD([[subQ2,-1.0]])],"derivedFrom":subQ1}),-1.0]])]});}
            var Q15;
            {var subQ0=sQuery(id+"F6.wireOp",EDGE,"E143");var subQ1=sQuery(id+"F6.wireOp",EDGE,"E121.0");var subQ2=makeQuery(id+"F6.imprint","INTERSECT",VERTEX,{"derivedFrom":[subQ1,subQ0]});Q15=makeQuery(id+"F6.imprint","IMPRINT",FACE,{"disambiguationData":[TD([[makeQuery(id+"F6.imprint","IMPRINT",EDGE,{"disambiguationData":[TD([[subQ2,-1.0]])],"derivedFrom":subQ1}),-1.0]])]});}
            var Q16;
            {var subQ0=sQuery(id+"F6.wireOp",EDGE,"E131.0");var subQ1=sQuery(id+"F6.wireOp",EDGE,"E121.0");var subQ2=makeQuery(id+"F6.imprint","INTERSECT",VERTEX,{"derivedFrom":[subQ1,subQ0]});Q16=makeQuery(id+"F6.imprint","IMPRINT",FACE,{"disambiguationData":[TD([[makeQuery(id+"F6.imprint","IMPRINT",EDGE,{"disambiguationData":[TD([[subQ2,-1.0]])],"derivedFrom":subQ1}),-1.0]])]});}
            var Q17;
            {var subQ0=sQuery(id+"F6.wireOp",EDGE,"E133");var subQ1=sQuery(id+"F6.wireOp",EDGE,"E121.0");var subQ2=makeQuery(id+"F6.imprint","INTERSECT",VERTEX,{"derivedFrom":[subQ1,subQ0]});Q17=makeQuery(id+"F6.imprint","IMPRINT",FACE,{"disambiguationData":[TD([[makeQuery(id+"F6.imprint","IMPRINT",EDGE,{"disambiguationData":[TD([[subQ2,-1.0]])],"derivedFrom":subQ1}),-1.0]])]});}
            var Q18;
            {var subQ0=sQuery(id+"F6.wireOp",EDGE,"E144.0");var subQ1=sQuery(id+"F6.wireOp",EDGE,"E121.0");var subQ2=makeQuery(id+"F6.imprint","INTERSECT",VERTEX,{"derivedFrom":[subQ1,subQ0]});Q18=makeQuery(id+"F6.imprint","IMPRINT",FACE,{"disambiguationData":[TD([[makeQuery(id+"F6.imprint","IMPRINT",EDGE,{"disambiguationData":[TD([[subQ2,-1.0]])],"derivedFrom":subQ1}),-1.0]])]});}
            var Q19;
            {var subQ0=sQuery(id+"F6.wireOp",EDGE,"E167");var subQ1=sQuery(id+"F6.wireOp",EDGE,"E121.0");var subQ2=makeQuery(id+"F6.imprint","INTERSECT",VERTEX,{"derivedFrom":[subQ1,subQ0]});Q19=makeQuery(id+"F6.imprint","IMPRINT",FACE,{"disambiguationData":[TD([[makeQuery(id+"F6.imprint","IMPRINT",EDGE,{"disambiguationData":[TD([[subQ2,-1.0]])],"derivedFrom":subQ1}),-1.0]])]});}
            var Q20;
            {var subQ0=sQuery(id+"F6.wireOp",EDGE,"E146.0");var subQ1=sQuery(id+"F6.wireOp",EDGE,"E121.0");var subQ2=makeQuery(id+"F6.imprint","INTERSECT",VERTEX,{"derivedFrom":[subQ1,subQ0]});Q20=makeQuery(id+"F6.imprint","IMPRINT",FACE,{"disambiguationData":[TD([[makeQuery(id+"F6.imprint","IMPRINT",EDGE,{"disambiguationData":[TD([[subQ2,-1.0]])],"derivedFrom":subQ1}),-1.0]])]});}
            var Q21;
            {var subQ0=sQuery(id+"F6.wireOp",EDGE,"E165");var subQ1=sQuery(id+"F6.wireOp",EDGE,"E121.0");var subQ2=makeQuery(id+"F6.imprint","INTERSECT",VERTEX,{"derivedFrom":[subQ1,subQ0]});Q21=makeQuery(id+"F6.imprint","IMPRINT",FACE,{"disambiguationData":[TD([[makeQuery(id+"F6.imprint","IMPRINT",EDGE,{"disambiguationData":[TD([[subQ2,-1.0]])],"derivedFrom":subQ1}),-1.0]])]});}
            var Q22;
            {var subQ3=sQuery(id+"F6.wireOp",EDGE,"E121.0");var subQ6=makeQuery(id+"F6.imprint","INTERSECT",VERTEX,{"derivedFrom":[subQ3,sQuery(id+"F6.wireOp",EDGE,"E163")]});Q22=makeQuery(id+"F6.imprint","IMPRINT",FACE,{"disambiguationData":[TD([[makeQuery(id+"F6.imprint","IMPRINT",EDGE,{"disambiguationData":[TD([[subQ6,1.0]])],"derivedFrom":subQ3}),1.0]])]});}
            var Q23;
            {var subQ1=sQuery(id+"F6.wireOp",EDGE,"E148.0");var subQ3=sQuery(id+"F6.wireOp",EDGE,"E121.0");var subQ4=makeQuery(id+"F6.imprint","INTERSECT",VERTEX,{"derivedFrom":[subQ3,subQ1]});Q23=makeQuery(id+"F6.imprint","IMPRINT",FACE,{"disambiguationData":[TD([[makeQuery(id+"F6.imprint","IMPRINT",EDGE,{"disambiguationData":[TD([[subQ4,-1.0]])],"derivedFrom":subQ3}),1.0]])]});}
            var Q24;
            {var subQ3=sQuery(id+"F6.wireOp",EDGE,"E121.0");var subQ6=sQuery(id+"F6.wireOp",EDGE,"E152.0");var subQ8=makeQuery(id+"F6.imprint","INTERSECT",VERTEX,{"derivedFrom":[subQ3,subQ6]});Q24=makeQuery(id+"F6.imprint","IMPRINT",FACE,{"disambiguationData":[TD([[makeQuery(id+"F6.imprint","IMPRINT",EDGE,{"disambiguationData":[TD([[subQ8,-1.0]])],"derivedFrom":subQ3}),1.0]])]});}
            var Q25;
            {var subQ3=sQuery(id+"F6.wireOp",EDGE,"E121.0");var subQ5=sQuery(id+"F6.wireOp",EDGE,"E154.0");var subQ7=makeQuery(id+"F6.imprint","INTERSECT",VERTEX,{"derivedFrom":[subQ3,subQ5]});Q25=makeQuery(id+"F6.imprint","IMPRINT",FACE,{"disambiguationData":[TD([[makeQuery(id+"F6.imprint","IMPRINT",EDGE,{"disambiguationData":[TD([[subQ7,-1.0]])],"derivedFrom":subQ3}),1.0]])]});}
            var Q26;
            {var subQ1=sQuery(id+"F6.wireOp",EDGE,"E137.0");var subQ3=sQuery(id+"F6.wireOp",EDGE,"E121.0");var subQ4=makeQuery(id+"F6.imprint","INTERSECT",VERTEX,{"derivedFrom":[subQ3,subQ1]});Q26=makeQuery(id+"F6.imprint","IMPRINT",FACE,{"disambiguationData":[TD([[makeQuery(id+"F6.imprint","IMPRINT",EDGE,{"disambiguationData":[TD([[subQ4,-1.0]])],"derivedFrom":subQ3}),1.0]])]});}
            var Q27;
            {var subQ1=sQuery(id+"F6.wireOp",EDGE,"E136.0");var subQ3=sQuery(id+"F6.wireOp",EDGE,"E121.0");var subQ4=makeQuery(id+"F6.imprint","INTERSECT",VERTEX,{"derivedFrom":[subQ3,subQ1]});Q27=makeQuery(id+"F6.imprint","IMPRINT",FACE,{"disambiguationData":[TD([[makeQuery(id+"F6.imprint","IMPRINT",EDGE,{"disambiguationData":[TD([[subQ4,-1.0]])],"derivedFrom":subQ3}),1.0]])]});}
            var Q28;
            {var subQ3=sQuery(id+"F6.wireOp",EDGE,"E121.0");var subQ5=sQuery(id+"F6.wireOp",EDGE,"E144.0");var subQ7=makeQuery(id+"F6.imprint","INTERSECT",VERTEX,{"derivedFrom":[subQ3,subQ5]});Q28=makeQuery(id+"F6.imprint","IMPRINT",FACE,{"disambiguationData":[TD([[makeQuery(id+"F6.imprint","IMPRINT",EDGE,{"disambiguationData":[TD([[subQ7,-1.0]])],"derivedFrom":subQ3}),1.0]])]});}
            var Q29;
            {var subQ3=sQuery(id+"F6.wireOp",EDGE,"E121.0");var subQ5=sQuery(id+"F6.wireOp",EDGE,"E146.0");var subQ7=makeQuery(id+"F6.imprint","INTERSECT",VERTEX,{"derivedFrom":[subQ3,subQ5]});Q29=makeQuery(id+"F6.imprint","IMPRINT",FACE,{"disambiguationData":[TD([[makeQuery(id+"F6.imprint","IMPRINT",EDGE,{"disambiguationData":[TD([[subQ7,-1.0]])],"derivedFrom":subQ3}),1.0]])]});}
            var Q30;
            {var subQ0=sQuery(id+"F6.wireOp",EDGE,"E126.0");var subQ1=sQuery(id+"F6.wireOp",EDGE,"E121.0");var subQ2=makeQuery(id+"F6.imprint","INTERSECT",VERTEX,{"derivedFrom":[subQ1,subQ0]});Q30=makeQuery(id+"F6.imprint","IMPRINT",FACE,{"disambiguationData":[TD([[makeQuery(id+"F6.imprint","IMPRINT",EDGE,{"disambiguationData":[TD([[subQ2,-1.0]])],"derivedFrom":subQ1}),1.0]])]});}
            var Q31;
            {var subQ1=sQuery(id+"F6.wireOp",EDGE,"E121.0");var subQ5=sQuery(id+"F6.wireOp",EDGE,"E122.0");var subQ6=makeQuery(id+"F6.imprint","INTERSECT",VERTEX,{"derivedFrom":[subQ1,subQ5]});Q31=makeQuery(id+"F6.imprint","IMPRINT",FACE,{"disambiguationData":[TD([[makeQuery(id+"F6.imprint","IMPRINT",EDGE,{"disambiguationData":[TD([[subQ6,-1.0]])],"derivedFrom":subQ1}),1.0]])]});}
            var Q32;
            {var subQ0=sQuery(id+"F6.wireOp",EDGE,"E131.0");var subQ1=sQuery(id+"F6.wireOp",EDGE,"E121.0");var subQ2=makeQuery(id+"F6.imprint","INTERSECT",VERTEX,{"derivedFrom":[subQ1,subQ0]});Q32=makeQuery(id+"F6.imprint","IMPRINT",FACE,{"disambiguationData":[TD([[makeQuery(id+"F6.imprint","IMPRINT",EDGE,{"disambiguationData":[TD([[subQ2,-1.0]])],"derivedFrom":subQ1}),1.0]])]});}
            var Q33;
            {var subQ0=sQuery(id+"F6.wireOp",EDGE,"E129");var subQ1=sQuery(id+"F6.wireOp",EDGE,"E126.0");var subQ2=makeQuery(id+"F6.imprint","INTERSECT",VERTEX,{"derivedFrom":[subQ1,subQ0]});Q33=makeQuery(id+"F6.imprint","IMPRINT",FACE,{"disambiguationData":[TD([[makeQuery(id+"F6.imprint","IMPRINT",EDGE,{"disambiguationData":[TD([[subQ2,-1.0]])],"derivedFrom":subQ1}),1.0]])]});}
            var Q34;
            {var subQ0=sQuery(id+"F6.wireOp",EDGE,"E124");var subQ4=sQuery(id+"F6.wireOp",EDGE,"E122.0");var subQ5=makeQuery(id+"F6.imprint","INTERSECT",VERTEX,{"derivedFrom":[subQ4,subQ0]});Q34=makeQuery(id+"F6.imprint","IMPRINT",FACE,{"disambiguationData":[TD([[makeQuery(id+"F6.imprint","IMPRINT",EDGE,{"disambiguationData":[TD([[subQ5,-1.0]])],"derivedFrom":subQ4}),1.0]])]});}
            var Q35;
            {var subQ0=sQuery(id+"F6.wireOp",EDGE,"E132");var subQ6=sQuery(id+"F6.wireOp",EDGE,"E130.0");var subQ7=makeQuery(id+"F6.imprint","INTERSECT",VERTEX,{"derivedFrom":[subQ6,subQ0]});Q35=makeQuery(id+"F6.imprint","IMPRINT",FACE,{"disambiguationData":[TD([[makeQuery(id+"F6.imprint","IMPRINT",EDGE,{"disambiguationData":[TD([[subQ7,1.0]])],"derivedFrom":subQ6}),1.0]])]});}
            extrude(context, id + "F9", {"entities" : qUnion([Q0, Q1, Q2, Q3, Q4, Q5, Q6, Q7, Q8, Q9, Q10, Q11, Q12, Q13, Q14, Q15, Q16, Q17, Q18, Q19, Q20, Q21, Q22, Q23, Q24, Q25, Q26, Q27, Q28, Q29, Q30, Q31, Q32, Q33, Q34, Q35]), "operationType" : NewBodyOperationType.ADD, "depth" : .5 * mm, "offsetDistance" : 25 * mm});
        }
    });
